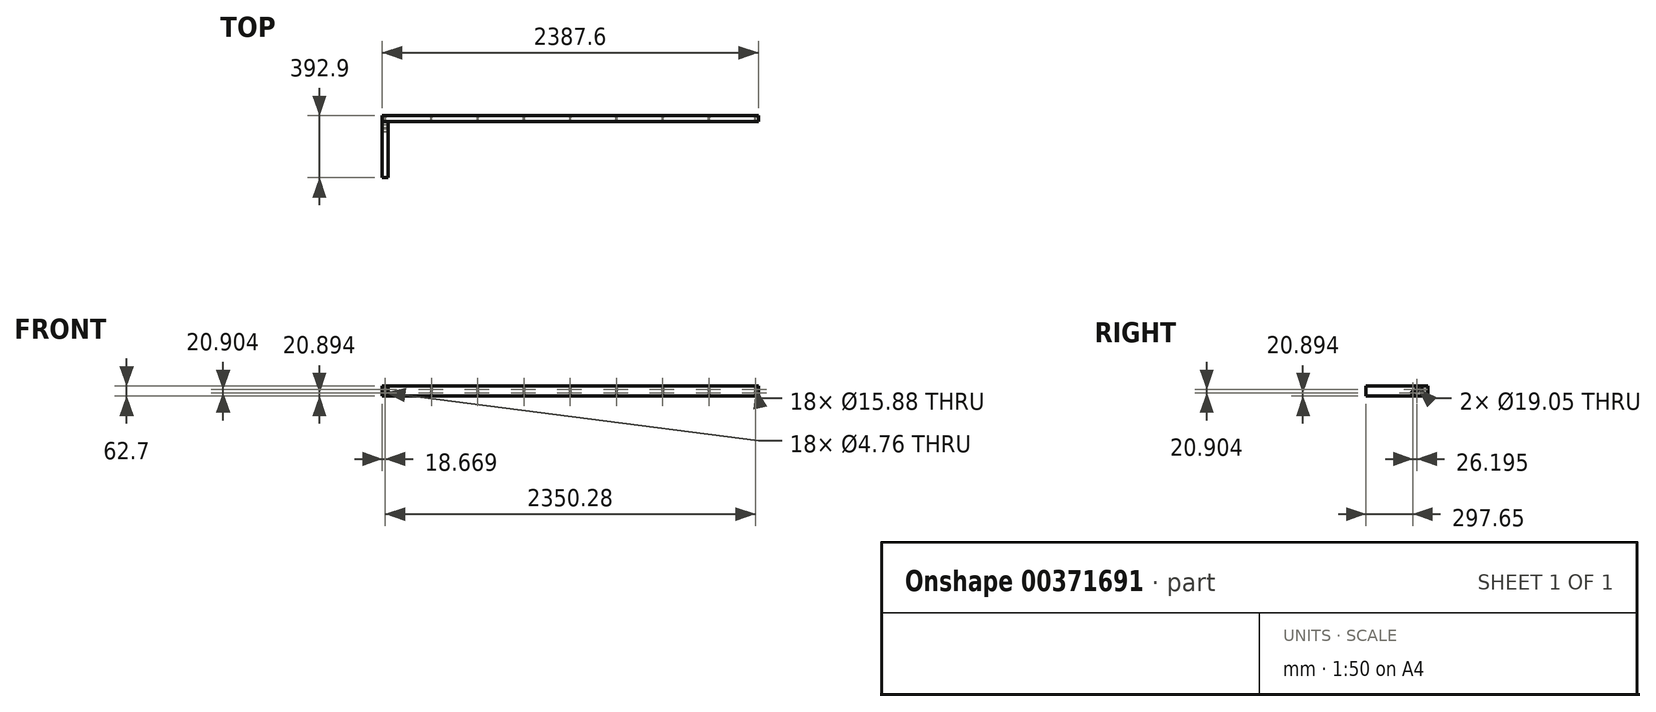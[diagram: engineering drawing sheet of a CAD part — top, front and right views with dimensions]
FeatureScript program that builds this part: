
annotation { "Feature Type Name" : "Feature", "Feature Type Description" : "" }
export const myFeature = defineFeature(function(context is Context, id is Id, definition is map)
    precondition{}
    {
        {
            var Q0;
            Q0=qCreatedBy(makeId("Front.planeOp"),FACE);
            var sketch = newSketch(context, id + "F0", { "sketchPlane" : qUnion([Q0])});
            skLineSegment(sketch, "E0.bottom", {"start": v(-1193.8, 31.35) * mm, "end": v(1193.8, 31.35) * mm});
            skLineSegment(sketch, "E0.top", {"start": v(-1193.8, -31.35) * mm, "end": v(1193.8, -31.35) * mm});
            skLineSegment(sketch, "E0.left", {"start": v(-1193.8, 31.35) * mm, "end": v(-1193.8, -31.35) * mm});
            skLineSegment(sketch, "E0.right", {"start": v(1193.8, 31.35) * mm, "end": v(1193.8, -31.35) * mm});
            skPoint(sketch, "E0.middle", {"position": v(0, 0) * mm});
            skSolve(sketch);
        }
        {
            var Q0;
            Q0=makeQuery(id+"F0.imprint","IMPRINT",FACE,{"disambiguationData":[TD([[makeQuery(id+"F0.imprint","IMPRINT",EDGE,{"derivedFrom":sQuery(id+"F0.wireOp",EDGE,"E0.bottom")}),-1.0]])]});
            extrude(context, id + "F1", {"entities" : qUnion([Q0]), "depth" : 37.3 * mm});
        }
        {
            var Q0;
            Q0=makeQuery(id+"F1.opExtrude","CAP_FACE",FACE,{"disambiguationData":[OSD([sQuery(id+"F0.wireOp",EDGE,"E0.bottom"),sQuery(id+"F0.wireOp",EDGE,"E0.top"),sQuery(id+"F0.wireOp",EDGE,"E0.left"),sQuery(id+"F0.wireOp",EDGE,"E0.right")])],"isStart":false});
            var sketch = newSketch(context, id + "F2", { "sketchPlane" : qUnion([Q0])});
            skLineSegment(sketch, "E1.bottom", {"start": v(-1193.8, 31.35) * mm, "end": v(-1156.5, 31.35) * mm});
            skLineSegment(sketch, "E1.top", {"start": v(-1193.8, -31.35) * mm, "end": v(-1156.5, -31.35) * mm});
            skLineSegment(sketch, "E1.left", {"start": v(-1193.8, 31.35) * mm, "end": v(-1193.8, -31.35) * mm});
            skLineSegment(sketch, "E1.right", {"start": v(-1156.5, 31.35) * mm, "end": v(-1156.5, -31.35) * mm});
            skSolve(sketch);
        }
        {
            var Q0;
            Q0=makeQuery(id+"F2.imprint","IMPRINT",FACE,{"disambiguationData":[TD([[makeQuery(id+"F2.imprint","IMPRINT",EDGE,{"derivedFrom":sQuery(id+"F2.wireOp",EDGE,"E1.bottom")}),-1.0]])]});
            extrude(context, id + "F3", {"entities" : qUnion([Q0]), "depth" : 355.6 * mm});
        }
        {
            var Q0;
            Q0=makeQuery(id+"F1.opExtrude","CAP_FACE",FACE,{"disambiguationData":[OSD([sQuery(id+"F0.wireOp",EDGE,"E0.bottom"),sQuery(id+"F0.wireOp",EDGE,"E0.top"),sQuery(id+"F0.wireOp",EDGE,"E0.left"),sQuery(id+"F0.wireOp",EDGE,"E0.right")])],"isStart":true});
            var sketch = newSketch(context, id + "F4", { "sketchPlane" : qUnion([Q0])});
            skPoint(sketch, "E2", {"position": v(-1175.14, 10.45) * mm});
            skPoint(sketch, "E3", {"position": v(-1175.14, -10.46) * mm});
            skPoint(sketch, "E4", {"position": v(-881.27, 10.45) * mm});
            skPoint(sketch, "E5", {"position": v(-881.27, -10.46) * mm});
            skPoint(sketch, "E6", {"position": v(-587.39, 10.45) * mm});
            skPoint(sketch, "E7", {"position": v(-587.39, -10.46) * mm});
            skPoint(sketch, "E8", {"position": v(-293.5, 10.45) * mm});
            skPoint(sketch, "E9", {"position": v(-293.5, -10.46) * mm});
            skPoint(sketch, "E10", {"position": v(0.37, 10.45) * mm});
            skPoint(sketch, "E11", {"position": v(0.37, -10.46) * mm});
            skPoint(sketch, "E12", {"position": v(294.25, 10.45) * mm});
            skPoint(sketch, "E13", {"position": v(294.25, -10.46) * mm});
            skPoint(sketch, "E14", {"position": v(588.12, 10.45) * mm});
            skPoint(sketch, "E15", {"position": v(588.12, -10.46) * mm});
            skPoint(sketch, "E16", {"position": v(882, 10.45) * mm});
            skPoint(sketch, "E17", {"position": v(882, -10.46) * mm});
            skPoint(sketch, "E18", {"position": v(1175.13, 10.45) * mm});
            skPoint(sketch, "E19", {"position": v(1175.13, -10.46) * mm});
            skSolve(sketch);
        }
        {
            var Q0;
            Q0=sQuery(id+"F4.wireOp",VERTEX,"E2");
            var Q1;
            Q1=sQuery(id+"F4.wireOp",VERTEX,"E3");
            var Q2;
            Q2=sQuery(id+"F4.wireOp",VERTEX,"E4");
            var Q3;
            Q3=sQuery(id+"F4.wireOp",VERTEX,"E5");
            var Q4;
            Q4=sQuery(id+"F4.wireOp",VERTEX,"E6");
            var Q5;
            Q5=sQuery(id+"F4.wireOp",VERTEX,"E7");
            var Q6;
            Q6=sQuery(id+"F4.wireOp",VERTEX,"E8");
            var Q7;
            Q7=sQuery(id+"F4.wireOp",VERTEX,"E9");
            var Q8;
            Q8=sQuery(id+"F4.wireOp",VERTEX,"E10");
            var Q9;
            Q9=sQuery(id+"F4.wireOp",VERTEX,"E11");
            var Q10;
            Q10=sQuery(id+"F4.wireOp",VERTEX,"E12");
            var Q11;
            Q11=sQuery(id+"F4.wireOp",VERTEX,"E13");
            var Q12;
            Q12=sQuery(id+"F4.wireOp",VERTEX,"E14");
            var Q13;
            Q13=sQuery(id+"F4.wireOp",VERTEX,"E15");
            var Q14;
            Q14=sQuery(id+"F4.wireOp",VERTEX,"E16");
            var Q15;
            Q15=sQuery(id+"F4.wireOp",VERTEX,"E17");
            var Q16;
            Q16=sQuery(id+"F4.wireOp",VERTEX,"E18");
            var Q17;
            Q17=sQuery(id+"F4.wireOp",VERTEX,"E19");
            var Q18;
            Q18=makeQuery(id+"F1.opExtrude","SWEPT_BODY",BODY,{"disambiguationData":[OSD([sQuery(id+"F0.wireOp",EDGE,"E0.bottom"),sQuery(id+"F0.wireOp",EDGE,"E0.top"),sQuery(id+"F0.wireOp",EDGE,"E0.left"),sQuery(id+"F0.wireOp",EDGE,"E0.right")])]});
            hole(context, id + "F5", {"style" : HoleStyle.SIMPLE, "endStyle" : HoleEndStyle.BLIND, "holeDiameter" : 15.88 * mm, "holeDepth" : 6.35 * mm, "isTappedThrough" : true, "tappedDepth" : 12.7 * mm, "tapClearance" : 3, "locations" : qUnion([Q0, Q1, Q2, Q3, Q4, Q5, Q6, Q7, Q8, Q9, Q10, Q11, Q12, Q13, Q14, Q15, Q16, Q17]), "scope" : qUnion([Q18])});
        }
        {
            var Q0;
            Q0=sQuery(id+"F4.wireOp",VERTEX,"E2");
            var Q1;
            Q1=sQuery(id+"F4.wireOp",VERTEX,"E3");
            var Q2;
            Q2=sQuery(id+"F4.wireOp",VERTEX,"E4");
            var Q3;
            Q3=sQuery(id+"F4.wireOp",VERTEX,"E5");
            var Q4;
            Q4=sQuery(id+"F4.wireOp",VERTEX,"E6");
            var Q5;
            Q5=sQuery(id+"F4.wireOp",VERTEX,"E7");
            var Q6;
            Q6=sQuery(id+"F4.wireOp",VERTEX,"E8");
            var Q7;
            Q7=sQuery(id+"F4.wireOp",VERTEX,"E9");
            var Q8;
            Q8=sQuery(id+"F4.wireOp",VERTEX,"E10");
            var Q9;
            Q9=sQuery(id+"F4.wireOp",VERTEX,"E11");
            var Q10;
            Q10=sQuery(id+"F4.wireOp",VERTEX,"E12");
            var Q11;
            Q11=sQuery(id+"F4.wireOp",VERTEX,"E13");
            var Q12;
            Q12=sQuery(id+"F4.wireOp",VERTEX,"E14");
            var Q13;
            Q13=sQuery(id+"F4.wireOp",VERTEX,"E15");
            var Q14;
            Q14=sQuery(id+"F4.wireOp",VERTEX,"E16");
            var Q15;
            Q15=sQuery(id+"F4.wireOp",VERTEX,"E17");
            var Q16;
            Q16=sQuery(id+"F4.wireOp",VERTEX,"E18");
            var Q17;
            Q17=sQuery(id+"F4.wireOp",VERTEX,"E19");
            var Q18;
            Q18=makeQuery(id+"F1.opExtrude","SWEPT_BODY",BODY,{"disambiguationData":[OSD([sQuery(id+"F0.wireOp",EDGE,"E0.bottom"),sQuery(id+"F0.wireOp",EDGE,"E0.top"),sQuery(id+"F0.wireOp",EDGE,"E0.left"),sQuery(id+"F0.wireOp",EDGE,"E0.right")])]});
            hole(context, id + "F6", {"style" : HoleStyle.SIMPLE, "endStyle" : HoleEndStyle.THROUGH, "holeDiameter" : 4.76 * mm, "isTappedThrough" : true, "tappedDepth" : 12.7 * mm, "tapClearance" : 3, "locations" : qUnion([Q0, Q1, Q2, Q3, Q4, Q5, Q6, Q7, Q8, Q9, Q10, Q11, Q12, Q13, Q14, Q15, Q16, Q17]), "scope" : qUnion([Q18])});
        }
        {
            var Q0;
            Q0=makeQuery(id+"F3.opExtrude","SWEPT_FACE",FACE,{"disambiguationData":[OSD([sQuery(id+"F2.wireOp",EDGE,"E1.left")])]});
            var sketch = newSketch(context, id + "F7", { "sketchPlane" : qUnion([Q0])});
            skPoint(sketch, "E20", {"position": v(69.05, 10.45) * mm});
            skPoint(sketch, "E21", {"position": v(95.25, -10.46) * mm});
            skSolve(sketch);
        }
        {
            var Q0;
            Q0=sQuery(id+"F7.wireOp",VERTEX,"E20");
            var Q1;
            Q1=sQuery(id+"F7.wireOp",VERTEX,"E21");
            var Q2;
            Q2=makeQuery(id+"F3.opExtrude","SWEPT_BODY",BODY,{"disambiguationData":[OSD([sQuery(id+"F2.wireOp",EDGE,"E1.bottom"),sQuery(id+"F2.wireOp",EDGE,"E1.top"),sQuery(id+"F2.wireOp",EDGE,"E1.left"),sQuery(id+"F2.wireOp",EDGE,"E1.right")])]});
            hole(context, id + "F8", {"style" : HoleStyle.SIMPLE, "endStyle" : HoleEndStyle.THROUGH, "holeDiameter" : 19.05 * mm, "isTappedThrough" : true, "tappedDepth" : 12.7 * mm, "tapClearance" : 3, "locations" : qUnion([Q0, Q1]), "scope" : qUnion([Q2])});
        }
        {
            var Q0;
            Q0=makeQuery(id+"F3.opExtrude","SWEPT_FACE",FACE,{"disambiguationData":[OSD([sQuery(id+"F2.wireOp",EDGE,"E1.left")])]});
            var sketch = newSketch(context, id + "F9", { "sketchPlane" : qUnion([Q0])});
            skCircle(sketch, "E22", {"center": v(69.05, 10.45) * mm, "radius": 9.52 * mm});
            skSolve(sketch);
        }
        {
            var Q0;
            Q0 = qSketchRegion(id + "F9", true);
            extrude(context, id + "F10", {"entities" : qUnion([Q0]), "oppositeDirection" : true, "depth" : 37.31 * mm});
        }
    });
